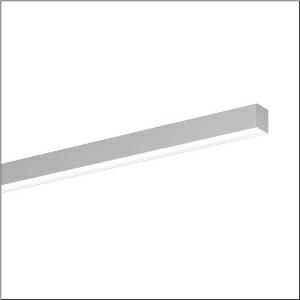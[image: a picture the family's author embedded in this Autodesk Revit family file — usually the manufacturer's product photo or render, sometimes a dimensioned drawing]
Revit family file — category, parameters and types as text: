
# Revit family: silica_r__21_51mx23dc4asb_a1ef
name_source: partatom
category: Lighting Fixtures
units: mm (PartAtom-declared; Revit-internal decimal feet)

## family parameters
Cut with Voids When Loaded = No
Host = Face
Light Source = No
Part Type = Normal
Room Calculation Point = No
Round Connector Dimension = Use Diameter
Shared = No

## types (1)
- --- (1 x LED, 8200 lm, 58.2 W, 4000K)
    Apparent Load = 58 VA
    CIE Flux Codes = 78 96 99 100 100
    Color Rendering = 80
    Color Temperature = 4000K
    Default Elevation = 1800 mm
    Description = Silica® 21, office luminaire, primary optical cover: prismatic diffuser, of PMMA, CAT 2 (L<= 3000cd/m²), light emission: direct distribution, primary light characteristic: symmetric, installation type: surface-mounted, LED, rated luminous flux: 8.200lm, luminous efficacy: 141lm/W, light colour: 840, colour temperature: 4000K, control gear: DALI 2, with terminal, 3+2-pole, max. 2.5mm², mains connection: 220..240V, AC, 50/60Hz, rated input power: 58.2W, luminaire housing, of aluminium, metallic grey (RAL 9006), length: 3.004mm, width: 53mm, height: 53mm, protection rating (complete): IP20, insulation class (complete): insulation class I (protective earthing), certification: CE, permissible operating ambient temperature: 0..+35°C, standard: EN 50419, packaging unit: 1 piece
    Height = 53 mm
    Lamp = 1 x LED
    Lamp Light Flux = 8200 lm
    Lamp Power = 58.2 W
    Lamp count = 1
    Length = 3004 mm
    Luminous efficacy = 141 lm/W
    Manufacturer = Siteco
    ModVariant = No
    Model = 51MX23DC4ASB
    Mounting Place = Ceiling
    Mounting Type = Surface mounted
    Number of Poles = 1
    OnlyDefault = Yes
    Power Factor = 1
    Product Name = Silica® 21
    Product group = office luminaire | ceiling mounted
    ProductGroupID = 302
    Protection Class = Protection class I
    Protection Degree = IP 20
    RLX_Detail_Level = 1
    RLX_Emergency_Light_Flux = 0 lm
    RLX_Emergency_Type = 0
    RLX_Emergency_Type_DB = No
    RlxData = <blob elided: 21221 chars, md5=15808b85>
    Socket = socket
    Standby Power = 0 W
    System Light Flux = 8200 lm
    System Power = 58 W
    Type Comments = factory setting: luminous flux: 100 % | dim-lin: 254 | 323 mA
    Type Image = l_1335933.jpg
    URL = http://relux.com
    VarID = @adj_119170
    Voltage = 0 V
    Weight = 0.00 kg
    Width = 53 mm

## geometry (parser evidence)
native form markers: Blend x4, Sweep x12
no freeform markers — native parametric forms only
